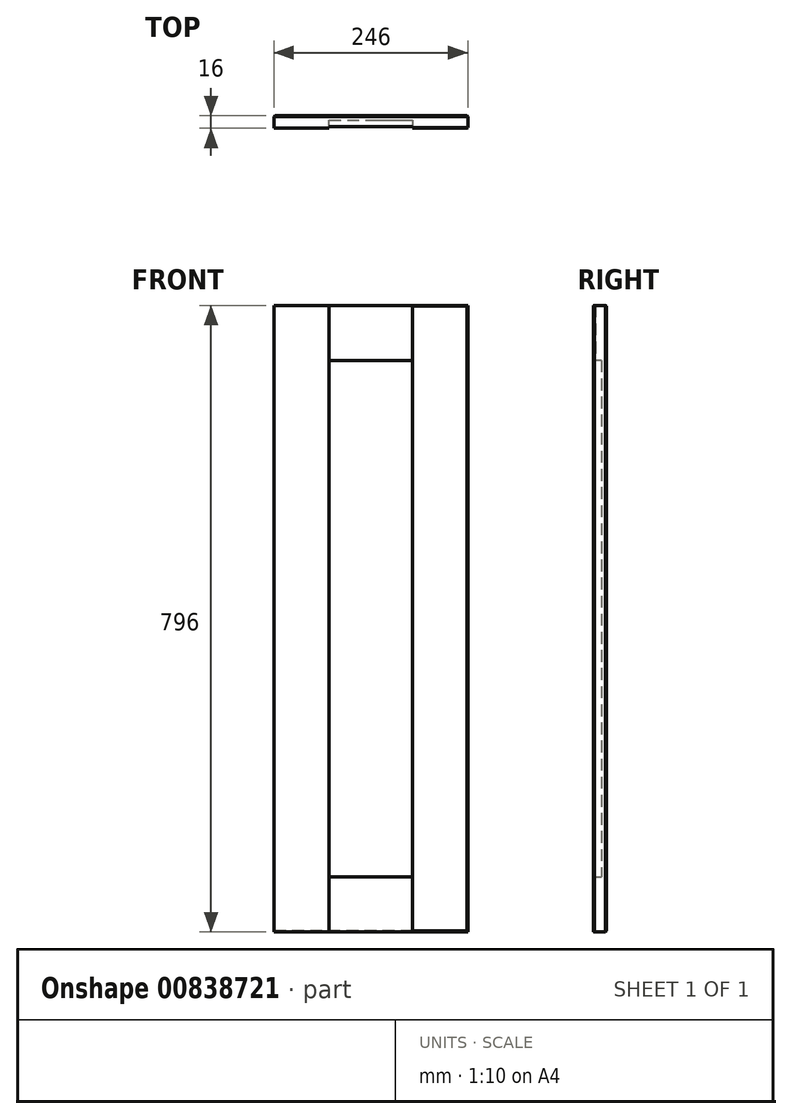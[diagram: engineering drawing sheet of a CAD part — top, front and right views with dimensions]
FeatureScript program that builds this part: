
annotation { "Feature Type Name" : "Feature", "Feature Type Description" : "" }
export const myFeature = defineFeature(function(context is Context, id is Id, definition is map)
    precondition{}
    {
        {
            var Q0;
            Q0=qCreatedBy(makeId("Front.planeOp"),FACE);
            var sketch = newSketch(context, id + "F0", { "sketchPlane" : qUnion([Q0])});
            skLineSegment(sketch, "E0.bottom", {"start": v(0, 0) * mm, "end": v(35.9, 0) * mm});
            skLineSegment(sketch, "E0.top", {"start": v(0, 30.12) * mm, "end": v(35.9, 30.12) * mm});
            skLineSegment(sketch, "E0.left", {"start": v(0, 0) * mm, "end": v(0, 30.12) * mm});
            skLineSegment(sketch, "E0.right", {"start": v(35.9, 0) * mm, "end": v(35.9, 30.12) * mm});
            skSolve(sketch);
        }
        {
            var Q0;
            Q0=makeQuery(id+"F0.imprint","IMPRINT",FACE,{"disambiguationData":[TD([[makeQuery(id+"F0.imprint","IMPRINT",EDGE,{"derivedFrom":sQuery(id+"F0.wireOp",EDGE,"E0.bottom")}),1.0]])]});
            extrude(context, id + "F1", {"entities" : qUnion([Q0]), "depth" : 16 * mm, "offsetDistance" : 25.4 * mm});
        }
        {
            var Q0;
            Q0=makeQuery(id+"F1.opExtrude","SWEPT_FACE",FACE,{"disambiguationData":[OSD([sQuery(id+"F0.wireOp",EDGE,"E0.left")])]});
            extrude(context, id + "F2", {"entities" : qUnion([Q0]), "operationType" : NewBodyOperationType.ADD, "oppositeDirection" : true, "depth" : 196 * mm, "offsetDistance" : 25 * mm});
        }
        {
            var Q0;
            {var subQ0=sQuery(id+"F0.wireOp",EDGE,"E0.bottom");Q0=makeQuery(id+"F2.boolean.opBoolean","MERGE",FACE,{"derivedFrom":[makeQuery(id+"F1.opExtrude","SWEPT_FACE",FACE,{"disambiguationData":[OSD([subQ0])]}),makeQuery(id+"F2.opExtrude","SWEPT_FACE",FACE,{"disambiguationData":[OSD([subQ0,sQuery(id+"F0.wireOp",EDGE,"E0.left")])]})]});}
            extrude(context, id + "F3", {"entities" : qUnion([Q0]), "operationType" : NewBodyOperationType.ADD, "oppositeDirection" : true, "depth" : 796 * mm, "offsetDistance" : 25 * mm});
        }
        {
            var Q0;
            {var subQ0=sQuery(id+"F0.wireOp",EDGE,"E0.left");var subQ1=sQuery(id+"F0.wireOp",EDGE,"E0.bottom");Q0=makeQuery(id+"F3.boolean.opBoolean","MERGE",FACE,{"derivedFrom":[makeQuery(id+"F2.boolean.opBoolean","MERGE",FACE,{"derivedFrom":[makeQuery(id+"F1.opExtrude","CAP_FACE",FACE,{"disambiguationData":[OSD([subQ1,sQuery(id+"F0.wireOp",EDGE,"E0.top"),subQ0,sQuery(id+"F0.wireOp",EDGE,"E0.right")])],"isStart":false}),makeQuery(id+"F2.opExtrude","SWEPT_FACE",FACE,{"disambiguationData":[OSD([subQ0]),TDD([makeQuery(id+"F1.opExtrude","CAP_EDGE",EDGE,{"disambiguationData":[OSD([subQ0])],"isStart":false})])]})]}),makeQuery(id+"F3.opExtrude","SWEPT_FACE",FACE,{"disambiguationData":[OSD([subQ1,subQ0]),TDD([makeQuery(id+"F2.boolean.opBoolean","MERGE",EDGE,{"derivedFrom":[makeQuery(id+"F1.opExtrude","CAP_EDGE",EDGE,{"disambiguationData":[OSD([subQ1])],"isStart":false}),makeQuery(id+"F2.opExtrude","SWEPT_EDGE",EDGE,{"disambiguationData":[OSD([subQ1,subQ0]),TDD([makeQuery(id+"F1.opExtrude","CAP_VERTEX",VERTEX,{"disambiguationData":[OSD([subQ1,subQ0])],"isStart":false})])]})]})])]})]});}
            var sketch = newSketch(context, id + "F4", { "sketchPlane" : qUnion([Q0])});
            skLineSegment(sketch, "E1.bottom", {"start": v(0, 796) * mm, "end": v(42.19, 796) * mm});
            skLineSegment(sketch, "E1.top", {"start": v(0, 751.57) * mm, "end": v(42.19, 751.57) * mm});
            skLineSegment(sketch, "E1.left", {"start": v(0, 796) * mm, "end": v(0, 751.57) * mm});
            skLineSegment(sketch, "E1.right", {"start": v(42.19, 796) * mm, "end": v(42.19, 751.57) * mm});
            skLineSegment(sketch, "E2.bottom", {"start": v(196, 796) * mm, "end": v(153.6, 796) * mm});
            skLineSegment(sketch, "E2.top", {"start": v(196, 746.75) * mm, "end": v(153.6, 746.75) * mm});
            skLineSegment(sketch, "E2.left", {"start": v(196, 796) * mm, "end": v(196, 746.75) * mm});
            skLineSegment(sketch, "E2.right", {"start": v(153.6, 796) * mm, "end": v(153.6, 746.75) * mm});
            skSolve(sketch);
        }
        {
            var Q0;
            Q0=makeQuery(id+"F4.imprint","IMPRINT",FACE,{"disambiguationData":[TD([[makeQuery(id+"F4.imprint","IMPRINT",EDGE,{"derivedFrom":sQuery(id+"F4.wireOp",EDGE,"E1.bottom")}),-1.0]])]});
            var Q1;
            Q1=makeQuery(id+"F4.imprint","IMPRINT",FACE,{"disambiguationData":[TD([[makeQuery(id+"F4.imprint","IMPRINT",EDGE,{"derivedFrom":sQuery(id+"F4.wireOp",EDGE,"E2.bottom")}),-1.0]])]});
            extrude(context, id + "F5", {"entities" : qUnion([Q0, Q1]), "operationType" : NewBodyOperationType.ADD, "depth" : 25 * mm, "offsetDistance" : 25 * mm});
        }
        {
            var Q0;
            {var subQ0=sQuery(id+"F0.wireOp",EDGE,"E0.left");var subQ1=sQuery(id+"F0.wireOp",EDGE,"E0.bottom");Q0=makeQuery(id+"F3.boolean.opBoolean","MERGE",FACE,{"derivedFrom":[makeQuery(id+"F2.boolean.opBoolean","MERGE",FACE,{"derivedFrom":[makeQuery(id+"F1.opExtrude","CAP_FACE",FACE,{"disambiguationData":[OSD([subQ1,sQuery(id+"F0.wireOp",EDGE,"E0.top"),subQ0,sQuery(id+"F0.wireOp",EDGE,"E0.right")])],"isStart":false}),makeQuery(id+"F2.opExtrude","SWEPT_FACE",FACE,{"disambiguationData":[OSD([subQ0]),TDD([makeQuery(id+"F1.opExtrude","CAP_EDGE",EDGE,{"disambiguationData":[OSD([subQ0])],"isStart":false})])]})]}),makeQuery(id+"F3.opExtrude","SWEPT_FACE",FACE,{"disambiguationData":[OSD([subQ1,subQ0]),TDD([makeQuery(id+"F2.boolean.opBoolean","MERGE",EDGE,{"derivedFrom":[makeQuery(id+"F1.opExtrude","CAP_EDGE",EDGE,{"disambiguationData":[OSD([subQ1])],"isStart":false}),makeQuery(id+"F2.opExtrude","SWEPT_EDGE",EDGE,{"disambiguationData":[OSD([subQ1,subQ0]),TDD([makeQuery(id+"F1.opExtrude","CAP_VERTEX",VERTEX,{"disambiguationData":[OSD([subQ1,subQ0])],"isStart":false})])]})]})])]})]});}
            var sketch = newSketch(context, id + "F6", { "sketchPlane" : qUnion([Q0])});
            skLineSegment(sketch, "E3.bottom", {"start": v(196, 0) * mm, "end": v(163.38, 0) * mm});
            skLineSegment(sketch, "E3.top", {"start": v(196, 46.55) * mm, "end": v(163.38, 46.55) * mm});
            skLineSegment(sketch, "E3.left", {"start": v(196, 0) * mm, "end": v(196, 46.55) * mm});
            skLineSegment(sketch, "E3.right", {"start": v(163.38, 0) * mm, "end": v(163.38, 46.55) * mm});
            skLineSegment(sketch, "E4.bottom", {"start": v(0, 0) * mm, "end": v(50.28, 0) * mm});
            skLineSegment(sketch, "E4.top", {"start": v(0, 44.4) * mm, "end": v(50.28, 44.4) * mm});
            skLineSegment(sketch, "E4.left", {"start": v(0, 0) * mm, "end": v(0, 44.4) * mm});
            skLineSegment(sketch, "E4.right", {"start": v(50.28, 0) * mm, "end": v(50.28, 44.4) * mm});
            skSolve(sketch);
        }
        {
            var Q0;
            Q0=makeQuery(id+"F6.imprint","IMPRINT",FACE,{"disambiguationData":[TD([[makeQuery(id+"F6.imprint","IMPRINT",EDGE,{"derivedFrom":sQuery(id+"F6.wireOp",EDGE,"E3.bottom")}),1.0]])]});
            var Q1;
            Q1=makeQuery(id+"F6.imprint","IMPRINT",FACE,{"disambiguationData":[TD([[makeQuery(id+"F6.imprint","IMPRINT",EDGE,{"derivedFrom":sQuery(id+"F6.wireOp",EDGE,"E4.bottom")}),1.0]])]});
            extrude(context, id + "F7", {"entities" : qUnion([Q0, Q1]), "operationType" : NewBodyOperationType.ADD, "depth" : 25 * mm, "offsetDistance" : 25 * mm});
        }
        {
            var Q0;
            Q0=makeQuery(id+"F7.opExtrude","SWEPT_FACE",FACE,{"disambiguationData":[OSD([sQuery(id+"F6.wireOp",EDGE,"E4.right")])]});
            extrude(context, id + "F8", {"entities" : qUnion([Q0]), "operationType" : NewBodyOperationType.ADD, "depth" : 19.72 * mm, "offsetDistance" : 25 * mm});
        }
        {
            var Q0;
            {var subQ0=sQuery(id+"F6.wireOp",EDGE,"E4.top");Q0=makeQuery(id+"F8.boolean.opBoolean","MERGE",FACE,{"derivedFrom":[makeQuery(id+"F7.opExtrude","SWEPT_FACE",FACE,{"disambiguationData":[OSD([subQ0])]}),makeQuery(id+"F8.opExtrude","SWEPT_FACE",FACE,{"disambiguationData":[OSD([subQ0,sQuery(id+"F6.wireOp",EDGE,"E4.right")])]})]});}
            extrude(context, id + "F9", {"entities" : qUnion([Q0]), "operationType" : NewBodyOperationType.ADD, "depth" : 25.6 * mm, "offsetDistance" : 25 * mm});
        }
        {
            var Q0;
            Q0=makeQuery(id+"F7.opExtrude","SWEPT_FACE",FACE,{"disambiguationData":[OSD([sQuery(id+"F6.wireOp",EDGE,"E3.right")])]});
            extrude(context, id + "F10", {"entities" : qUnion([Q0]), "operationType" : NewBodyOperationType.ADD, "depth" : 37.38 * mm, "offsetDistance" : 25 * mm});
        }
        {
            var Q0;
            {var subQ0=sQuery(id+"F6.wireOp",EDGE,"E3.top");Q0=makeQuery(id+"F10.boolean.opBoolean","MERGE",FACE,{"derivedFrom":[makeQuery(id+"F7.opExtrude","SWEPT_FACE",FACE,{"disambiguationData":[OSD([subQ0])]}),makeQuery(id+"F10.opExtrude","SWEPT_FACE",FACE,{"disambiguationData":[OSD([subQ0,sQuery(id+"F6.wireOp",EDGE,"E3.right")])]})]});}
            extrude(context, id + "F11", {"entities" : qUnion([Q0]), "operationType" : NewBodyOperationType.ADD, "depth" : 23.45 * mm, "offsetDistance" : 25 * mm});
        }
        {
            var Q0;
            Q0=makeQuery(id+"F5.opExtrude","SWEPT_FACE",FACE,{"disambiguationData":[OSD([sQuery(id+"F4.wireOp",EDGE,"E1.right")])]});
            extrude(context, id + "F12", {"entities" : qUnion([Q0]), "operationType" : NewBodyOperationType.ADD, "depth" : 27.8 * mm, "offsetDistance" : 25 * mm});
        }
        {
            var Q0;
            {var subQ0=sQuery(id+"F4.wireOp",EDGE,"E1.top");Q0=makeQuery(id+"F12.boolean.opBoolean","MERGE",FACE,{"derivedFrom":[makeQuery(id+"F5.opExtrude","SWEPT_FACE",FACE,{"disambiguationData":[OSD([subQ0])]}),makeQuery(id+"F12.opExtrude","SWEPT_FACE",FACE,{"disambiguationData":[OSD([subQ0,sQuery(id+"F4.wireOp",EDGE,"E1.right")])]})]});}
            extrude(context, id + "F13", {"entities" : qUnion([Q0]), "operationType" : NewBodyOperationType.ADD, "depth" : 25.57 * mm, "offsetDistance" : 25 * mm});
        }
        {
            var Q0;
            Q0=makeQuery(id+"F5.opExtrude","SWEPT_FACE",FACE,{"disambiguationData":[OSD([sQuery(id+"F4.wireOp",EDGE,"E2.top")])]});
            extrude(context, id + "F14", {"entities" : qUnion([Q0]), "operationType" : NewBodyOperationType.ADD, "depth" : 20.75 * mm, "offsetDistance" : 25 * mm});
        }
        {
            var Q0;
            {var subQ0=sQuery(id+"F4.wireOp",EDGE,"E2.right");Q0=makeQuery(id+"F14.boolean.opBoolean","MERGE",FACE,{"derivedFrom":[makeQuery(id+"F5.opExtrude","SWEPT_FACE",FACE,{"disambiguationData":[OSD([subQ0])]}),makeQuery(id+"F14.opExtrude","SWEPT_FACE",FACE,{"disambiguationData":[OSD([sQuery(id+"F4.wireOp",EDGE,"E2.top"),subQ0])]})]});}
            extrude(context, id + "F15", {"entities" : qUnion([Q0]), "operationType" : NewBodyOperationType.ADD, "depth" : 27.6 * mm, "offsetDistance" : 25 * mm});
        }
        {
            var Q0;
            {var subQ0=sQuery(id+"F0.wireOp",EDGE,"E0.left");var subQ1=sQuery(id+"F0.wireOp",EDGE,"E0.bottom");Q0=makeQuery(id+"F3.boolean.opBoolean","MERGE",FACE,{"derivedFrom":[makeQuery(id+"F2.boolean.opBoolean","MERGE",FACE,{"derivedFrom":[makeQuery(id+"F1.opExtrude","CAP_FACE",FACE,{"disambiguationData":[OSD([subQ1,sQuery(id+"F0.wireOp",EDGE,"E0.top"),subQ0,sQuery(id+"F0.wireOp",EDGE,"E0.right")])],"isStart":false}),makeQuery(id+"F2.opExtrude","SWEPT_FACE",FACE,{"disambiguationData":[OSD([subQ0]),TDD([makeQuery(id+"F1.opExtrude","CAP_EDGE",EDGE,{"disambiguationData":[OSD([subQ0])],"isStart":false})])]})]}),makeQuery(id+"F3.opExtrude","SWEPT_FACE",FACE,{"disambiguationData":[OSD([subQ1,subQ0]),TDD([makeQuery(id+"F2.boolean.opBoolean","MERGE",EDGE,{"derivedFrom":[makeQuery(id+"F1.opExtrude","CAP_EDGE",EDGE,{"disambiguationData":[OSD([subQ1])],"isStart":false}),makeQuery(id+"F2.opExtrude","SWEPT_EDGE",EDGE,{"disambiguationData":[OSD([subQ1,subQ0]),TDD([makeQuery(id+"F1.opExtrude","CAP_VERTEX",VERTEX,{"disambiguationData":[OSD([subQ1,subQ0])],"isStart":false})])]})]})])]})]});}
            var sketch = newSketch(context, id + "F16", { "sketchPlane" : qUnion([Q0])});
            skLineSegment(sketch, "E5.bottom", {"start": v(70, 726) * mm, "end": v(126, 726) * mm});
            skLineSegment(sketch, "E5.top", {"start": v(70, 70) * mm, "end": v(126, 70) * mm});
            skLineSegment(sketch, "E5.left", {"start": v(70, 726) * mm, "end": v(70, 70) * mm});
            skLineSegment(sketch, "E5.right", {"start": v(126, 726) * mm, "end": v(126, 70) * mm});
            skSolve(sketch);
        }
        {
            var Q0;
            Q0=makeQuery(id+"F16.imprint","IMPRINT",FACE,{"disambiguationData":[TD([[makeQuery(id+"F16.imprint","IMPRINT",EDGE,{"derivedFrom":sQuery(id+"F16.wireOp",EDGE,"E5.top")}),1.0]])]});
            extrude(context, id + "F17", {"entities" : qUnion([Q0]), "operationType" : NewBodyOperationType.REMOVE, "oppositeDirection" : true, "depth" : 10 * mm, "offsetDistance" : 25 * mm});
        }
        {
            var Q0;
            {var subQ2=sQuery(id+"F0.wireOp",EDGE,"E0.left");var subQ3=sQuery(id+"F0.wireOp",EDGE,"E0.bottom");var subQ4=makeQuery(id+"F1.opExtrude","CAP_FACE",FACE,{"disambiguationData":[OSD([subQ3,sQuery(id+"F0.wireOp",EDGE,"E0.top"),subQ2,sQuery(id+"F0.wireOp",EDGE,"E0.right")])],"isStart":false});var subQ7=makeQuery(id+"F3.opExtrude","SWEPT_FACE",FACE,{"disambiguationData":[OSD([subQ3,subQ2]),TDD([makeQuery(id+"F2.boolean.opBoolean","MERGE",EDGE,{"derivedFrom":[makeQuery(id+"F1.opExtrude","CAP_EDGE",EDGE,{"disambiguationData":[OSD([subQ3])],"isStart":false}),makeQuery(id+"F2.opExtrude","SWEPT_EDGE",EDGE,{"disambiguationData":[OSD([subQ3,subQ2]),TDD([makeQuery(id+"F1.opExtrude","CAP_VERTEX",VERTEX,{"disambiguationData":[OSD([subQ3,subQ2])],"isStart":false})])]})]})])]});var subQ8=makeQuery(id+"F2.opExtrude","SWEPT_FACE",FACE,{"disambiguationData":[OSD([subQ2]),TDD([makeQuery(id+"F1.opExtrude","CAP_EDGE",EDGE,{"disambiguationData":[OSD([subQ2])],"isStart":false})])]});Q0=makeQuery(id+"F17.boolean.opBoolean","SPLIT",FACE,{"disambiguationData":[TD([makeQuery(id+"F1.opExtrude","SWEPT_FACE",FACE,{"disambiguationData":[OSD([subQ3])]})])],"derivedFrom":makeQuery(id+"F3.boolean.opBoolean","MERGE",FACE,{"derivedFrom":[makeQuery(id+"F2.boolean.opBoolean","MERGE",FACE,{"derivedFrom":[subQ4,subQ8]}),subQ7]})});}
            var Q1;
            {var subQ2=sQuery(id+"F4.wireOp",EDGE,"E1.bottom");var subQ3=sQuery(id+"F0.wireOp",EDGE,"E0.left");var subQ4=sQuery(id+"F0.wireOp",EDGE,"E0.bottom");var subQ6=makeQuery(id+"F1.opExtrude","CAP_FACE",FACE,{"disambiguationData":[OSD([subQ4,sQuery(id+"F0.wireOp",EDGE,"E0.top"),subQ3,sQuery(id+"F0.wireOp",EDGE,"E0.right")])],"isStart":false});var subQ7=makeQuery(id+"F2.opExtrude","SWEPT_FACE",FACE,{"disambiguationData":[OSD([subQ3]),TDD([makeQuery(id+"F1.opExtrude","CAP_EDGE",EDGE,{"disambiguationData":[OSD([subQ3])],"isStart":false})])]});var subQ8=makeQuery(id+"F3.opExtrude","SWEPT_FACE",FACE,{"disambiguationData":[OSD([subQ4,subQ3]),TDD([makeQuery(id+"F2.boolean.opBoolean","MERGE",EDGE,{"derivedFrom":[makeQuery(id+"F1.opExtrude","CAP_EDGE",EDGE,{"disambiguationData":[OSD([subQ4])],"isStart":false}),makeQuery(id+"F2.opExtrude","SWEPT_EDGE",EDGE,{"disambiguationData":[OSD([subQ4,subQ3]),TDD([makeQuery(id+"F1.opExtrude","CAP_VERTEX",VERTEX,{"disambiguationData":[OSD([subQ4,subQ3])],"isStart":false})])]})]})])]});Q1=makeQuery(id+"F17.boolean.opBoolean","SPLIT",FACE,{"disambiguationData":[TD([makeQuery(id+"F5.opExtrude","SWEPT_FACE",FACE,{"disambiguationData":[OSD([subQ2])]})])],"derivedFrom":makeQuery(id+"F3.boolean.opBoolean","MERGE",FACE,{"derivedFrom":[makeQuery(id+"F2.boolean.opBoolean","MERGE",FACE,{"derivedFrom":[subQ6,subQ7]}),subQ8]})});}
            extrude(context, id + "F18", {"entities" : qUnion([Q0, Q1]), "operationType" : NewBodyOperationType.REMOVE, "oppositeDirection" : true, "depth" : 2 * mm, "offsetDistance" : 25 * mm});
        }
        {
            var Q0;
            {var subQ0=sQuery(id+"F4.wireOp",EDGE,"E1.right");var subQ1=sQuery(id+"F4.wireOp",EDGE,"E1.top");Q0=makeQuery(id+"F13.boolean.opBoolean","MERGE",FACE,{"derivedFrom":[makeQuery(id+"F12.boolean.opBoolean","MERGE",FACE,{"derivedFrom":[makeQuery(id+"F5.opExtrude","CAP_FACE",FACE,{"disambiguationData":[OSD([sQuery(id+"F4.wireOp",EDGE,"E1.bottom"),subQ1,sQuery(id+"F4.wireOp",EDGE,"E1.left"),subQ0])],"isStart":false}),makeQuery(id+"F12.opExtrude","SWEPT_FACE",FACE,{"disambiguationData":[OSD([subQ0]),TDD([makeQuery(id+"F5.opExtrude","CAP_EDGE",EDGE,{"disambiguationData":[OSD([subQ0])],"isStart":false})])]})]}),makeQuery(id+"F13.opExtrude","SWEPT_FACE",FACE,{"disambiguationData":[OSD([subQ1,subQ0]),TDD([makeQuery(id+"F12.boolean.opBoolean","MERGE",EDGE,{"derivedFrom":[makeQuery(id+"F5.opExtrude","CAP_EDGE",EDGE,{"disambiguationData":[OSD([subQ1])],"isStart":false}),makeQuery(id+"F12.opExtrude","SWEPT_EDGE",EDGE,{"disambiguationData":[OSD([subQ1,subQ0]),TDD([makeQuery(id+"F5.opExtrude","CAP_VERTEX",VERTEX,{"disambiguationData":[OSD([subQ1,subQ0])],"isStart":false})])]})]})])]})]});}
            var Q1;
            {var subQ0=sQuery(id+"F4.wireOp",EDGE,"E2.right");var subQ1=sQuery(id+"F4.wireOp",EDGE,"E2.top");Q1=makeQuery(id+"F15.boolean.opBoolean","MERGE",FACE,{"derivedFrom":[makeQuery(id+"F14.boolean.opBoolean","MERGE",FACE,{"derivedFrom":[makeQuery(id+"F5.opExtrude","CAP_FACE",FACE,{"disambiguationData":[OSD([sQuery(id+"F4.wireOp",EDGE,"E2.bottom"),subQ1,sQuery(id+"F4.wireOp",EDGE,"E2.left"),subQ0])],"isStart":false}),makeQuery(id+"F14.opExtrude","SWEPT_FACE",FACE,{"disambiguationData":[OSD([subQ1]),TDD([makeQuery(id+"F5.opExtrude","CAP_EDGE",EDGE,{"disambiguationData":[OSD([subQ1])],"isStart":false})])]})]}),makeQuery(id+"F15.opExtrude","SWEPT_FACE",FACE,{"disambiguationData":[OSD([subQ1,subQ0]),TDD([makeQuery(id+"F14.boolean.opBoolean","MERGE",EDGE,{"derivedFrom":[makeQuery(id+"F5.opExtrude","CAP_EDGE",EDGE,{"disambiguationData":[OSD([subQ0])],"isStart":false}),makeQuery(id+"F14.opExtrude","SWEPT_EDGE",EDGE,{"disambiguationData":[OSD([subQ1,subQ0]),TDD([makeQuery(id+"F5.opExtrude","CAP_VERTEX",VERTEX,{"disambiguationData":[OSD([subQ1,subQ0])],"isStart":false})])]})]})])]})]});}
            var Q2;
            {var subQ0=sQuery(id+"F6.wireOp",EDGE,"E4.right");var subQ1=sQuery(id+"F6.wireOp",EDGE,"E4.top");Q2=makeQuery(id+"F9.boolean.opBoolean","MERGE",FACE,{"derivedFrom":[makeQuery(id+"F8.boolean.opBoolean","MERGE",FACE,{"derivedFrom":[makeQuery(id+"F7.opExtrude","CAP_FACE",FACE,{"disambiguationData":[OSD([sQuery(id+"F6.wireOp",EDGE,"E4.bottom"),subQ1,sQuery(id+"F6.wireOp",EDGE,"E4.left"),subQ0])],"isStart":false}),makeQuery(id+"F8.opExtrude","SWEPT_FACE",FACE,{"disambiguationData":[OSD([subQ0]),TDD([makeQuery(id+"F7.opExtrude","CAP_EDGE",EDGE,{"disambiguationData":[OSD([subQ0])],"isStart":false})])]})]}),makeQuery(id+"F9.opExtrude","SWEPT_FACE",FACE,{"disambiguationData":[OSD([subQ1,subQ0]),TDD([makeQuery(id+"F8.boolean.opBoolean","MERGE",EDGE,{"derivedFrom":[makeQuery(id+"F7.opExtrude","CAP_EDGE",EDGE,{"disambiguationData":[OSD([subQ1])],"isStart":false}),makeQuery(id+"F8.opExtrude","SWEPT_EDGE",EDGE,{"disambiguationData":[OSD([subQ1,subQ0]),TDD([makeQuery(id+"F7.opExtrude","CAP_VERTEX",VERTEX,{"disambiguationData":[OSD([subQ1,subQ0])],"isStart":false})])]})]})])]})]});}
            var Q3;
            {var subQ0=sQuery(id+"F6.wireOp",EDGE,"E3.right");var subQ1=sQuery(id+"F6.wireOp",EDGE,"E3.top");Q3=makeQuery(id+"F11.boolean.opBoolean","MERGE",FACE,{"derivedFrom":[makeQuery(id+"F10.boolean.opBoolean","MERGE",FACE,{"derivedFrom":[makeQuery(id+"F7.opExtrude","CAP_FACE",FACE,{"disambiguationData":[OSD([sQuery(id+"F6.wireOp",EDGE,"E3.bottom"),subQ1,sQuery(id+"F6.wireOp",EDGE,"E3.left"),subQ0])],"isStart":false}),makeQuery(id+"F10.opExtrude","SWEPT_FACE",FACE,{"disambiguationData":[OSD([subQ0]),TDD([makeQuery(id+"F7.opExtrude","CAP_EDGE",EDGE,{"disambiguationData":[OSD([subQ0])],"isStart":false})])]})]}),makeQuery(id+"F11.opExtrude","SWEPT_FACE",FACE,{"disambiguationData":[OSD([subQ1,subQ0]),TDD([makeQuery(id+"F10.boolean.opBoolean","MERGE",EDGE,{"derivedFrom":[makeQuery(id+"F7.opExtrude","CAP_EDGE",EDGE,{"disambiguationData":[OSD([subQ1])],"isStart":false}),makeQuery(id+"F10.opExtrude","SWEPT_EDGE",EDGE,{"disambiguationData":[OSD([subQ1,subQ0]),TDD([makeQuery(id+"F7.opExtrude","CAP_VERTEX",VERTEX,{"disambiguationData":[OSD([subQ1,subQ0])],"isStart":false})])]})]})])]})]});}
            extrude(context, id + "F19", {"entities" : qUnion([Q0, Q1, Q2, Q3]), "operationType" : NewBodyOperationType.REMOVE, "oppositeDirection" : true, "depth" : 25 * mm, "offsetDistance" : 25 * mm});
        }
        {
            var Q0;
            {var subQ0=sQuery(id+"F4.wireOp",EDGE,"E2.left");var subQ1=sQuery(id+"F0.wireOp",EDGE,"E0.left");var subQ2=sQuery(id+"F0.wireOp",EDGE,"E0.bottom");var subQ3=sQuery(id+"F6.wireOp",EDGE,"E3.left");Q0=makeQuery(id+"F14.boolean.opBoolean","MERGE",FACE,{"derivedFrom":[makeQuery(id+"F11.boolean.opBoolean","MERGE",FACE,{"derivedFrom":[makeQuery(id+"F7.boolean.opBoolean","MERGE",FACE,{"derivedFrom":[makeQuery(id+"F5.boolean.opBoolean","MERGE",FACE,{"derivedFrom":[makeQuery(id+"F3.boolean.opBoolean","MERGE",FACE,{"derivedFrom":[makeQuery(id+"F2.opExtrude","CAP_FACE",FACE,{"disambiguationData":[OSD([subQ1])],"isStart":false}),makeQuery(id+"F3.opExtrude","SWEPT_FACE",FACE,{"disambiguationData":[OSD([subQ2,subQ1]),TDD([makeQuery(id+"F2.opExtrude","CAP_EDGE",EDGE,{"disambiguationData":[OSD([subQ2,subQ1])],"isStart":false})])]})]}),makeQuery(id+"F5.opExtrude","SWEPT_FACE",FACE,{"disambiguationData":[OSD([subQ0])]})]}),makeQuery(id+"F7.opExtrude","SWEPT_FACE",FACE,{"disambiguationData":[OSD([subQ3])]})]}),makeQuery(id+"F11.opExtrude","SWEPT_FACE",FACE,{"disambiguationData":[OSD([subQ2,subQ1,sQuery(id+"F6.wireOp",EDGE,"E3.top"),subQ3])]})]}),makeQuery(id+"F14.opExtrude","SWEPT_FACE",FACE,{"disambiguationData":[OSD([subQ2,subQ1,sQuery(id+"F4.wireOp",EDGE,"E2.top"),subQ0])]})]});}
            extrude(context, id + "F20", {"entities" : qUnion([Q0]), "operationType" : NewBodyOperationType.ADD, "depth" : 50 * mm, "offsetDistance" : 25 * mm});
        }
        {
            var Q0;
            {var subQ0=sQuery(id+"F4.wireOp",EDGE,"E2.right");var subQ1=sQuery(id+"F4.wireOp",EDGE,"E2.top");Q0=makeQuery(id+"F18.boolean.opBoolean","MERGE",FACE,{"derivedFrom":[makeQuery(id+"F15.opExtrude","CAP_FACE",FACE,{"disambiguationData":[OSD([subQ1,subQ0])],"isStart":false}),makeQuery(id+"F18.opExtrude","SWEPT_FACE",FACE,{"disambiguationData":[OSD([subQ1,subQ0])]})]});}
            var Q1;
            {var subQ0=sQuery(id+"F6.wireOp",EDGE,"E3.right");var subQ1=sQuery(id+"F6.wireOp",EDGE,"E3.top");Q1=makeQuery(id+"F18.boolean.opBoolean","MERGE",FACE,{"derivedFrom":[makeQuery(id+"F11.boolean.opBoolean","MERGE",FACE,{"derivedFrom":[makeQuery(id+"F10.opExtrude","CAP_FACE",FACE,{"disambiguationData":[OSD([subQ0])],"isStart":false}),makeQuery(id+"F11.opExtrude","SWEPT_FACE",FACE,{"disambiguationData":[OSD([subQ1,subQ0]),TDD([makeQuery(id+"F10.opExtrude","CAP_EDGE",EDGE,{"disambiguationData":[OSD([subQ1,subQ0])],"isStart":false})])]})]}),makeQuery(id+"F17.boolean.opBoolean","COPY",FACE,{"derivedFrom":makeQuery(id+"F17.opExtrude","SWEPT_FACE",FACE,{"disambiguationData":[OSD([sQuery(id+"F16.wireOp",EDGE,"E5.right")])]})}),makeQuery(id+"F18.opExtrude","SWEPT_FACE",FACE,{"disambiguationData":[OSD([subQ1,subQ0])]})]});}
            extrude(context, id + "F21", {"entities" : qUnion([Q0, Q1]), "operationType" : NewBodyOperationType.REMOVE, "oppositeDirection" : true, "depth" : 50 * mm, "offsetDistance" : 25 * mm});
        }
        {
            var Q0;
            Q0=makeQuery(id+"F19.boolean.opBoolean","COPY",EDGE,{"derivedFrom":makeQuery(id+"F19.opExtrude","CAP_EDGE",EDGE,{"disambiguationData":[OSD([sQuery(id+"F0.wireOp",EDGE,"E0.bottom"),sQuery(id+"F0.wireOp",EDGE,"E0.left"),sQuery(id+"F4.wireOp",EDGE,"E1.bottom"),sQuery(id+"F4.wireOp",EDGE,"E1.right")])],"isStart":false})});
            var Q1;
            {var subQ0=sQuery(id+"F4.wireOp",EDGE,"E2.bottom");Q1=makeQuery(id+"F20.boolean.opBoolean","MERGE",EDGE,{"derivedFrom":[makeQuery(id+"F19.boolean.opBoolean","COPY",EDGE,{"derivedFrom":makeQuery(id+"F19.opExtrude","CAP_EDGE",EDGE,{"disambiguationData":[OSD([sQuery(id+"F0.wireOp",EDGE,"E0.bottom"),sQuery(id+"F0.wireOp",EDGE,"E0.left"),subQ0,sQuery(id+"F4.wireOp",EDGE,"E2.right")])],"isStart":false})}),makeQuery(id+"F20.opExtrude","SWEPT_EDGE",EDGE,{"disambiguationData":[OSD([subQ0,sQuery(id+"F4.wireOp",EDGE,"E2.left")])]})]});}
            var Q2;
            Q2=makeQuery(id+"F20.opExtrude","CAP_EDGE",EDGE,{"disambiguationData":[OSD([sQuery(id+"F0.wireOp",EDGE,"E0.bottom"),sQuery(id+"F0.wireOp",EDGE,"E0.left"),sQuery(id+"F4.wireOp",EDGE,"E2.top"),sQuery(id+"F4.wireOp",EDGE,"E2.left"),sQuery(id+"F6.wireOp",EDGE,"E3.top"),sQuery(id+"F6.wireOp",EDGE,"E3.left")])],"isStart":false});
            var Q3;
            {var subQ0=sQuery(id+"F0.wireOp",EDGE,"E0.left");var subQ1=sQuery(id+"F0.wireOp",EDGE,"E0.bottom");Q3=makeQuery(id+"F19.boolean.opBoolean","MERGE",EDGE,{"derivedFrom":[makeQuery(id+"F3.boolean.opBoolean","MERGE",EDGE,{"derivedFrom":[makeQuery(id+"F1.opExtrude","CAP_EDGE",EDGE,{"disambiguationData":[OSD([subQ0])],"isStart":false}),makeQuery(id+"F3.opExtrude","SWEPT_EDGE",EDGE,{"disambiguationData":[OSD([subQ1,subQ0]),TDD([makeQuery(id+"F1.opExtrude","CAP_VERTEX",VERTEX,{"disambiguationData":[OSD([subQ1,subQ0])],"isStart":false})])]})]}),makeQuery(id+"F19.opExtrude","CAP_EDGE",EDGE,{"disambiguationData":[OSD([subQ1,subQ0,sQuery(id+"F6.wireOp",EDGE,"E4.top"),sQuery(id+"F6.wireOp",EDGE,"E4.left")])],"isStart":false}),makeQuery(id+"F19.opExtrude","CAP_EDGE",EDGE,{"disambiguationData":[OSD([subQ1,subQ0,sQuery(id+"F4.wireOp",EDGE,"E1.top"),sQuery(id+"F4.wireOp",EDGE,"E1.left")])],"isStart":false})]});}
            var Q4;
            {var subQ0=sQuery(id+"F6.wireOp",EDGE,"E3.bottom");Q4=makeQuery(id+"F20.boolean.opBoolean","MERGE",EDGE,{"derivedFrom":[makeQuery(id+"F19.boolean.opBoolean","COPY",EDGE,{"derivedFrom":makeQuery(id+"F19.opExtrude","CAP_EDGE",EDGE,{"disambiguationData":[OSD([sQuery(id+"F0.wireOp",EDGE,"E0.bottom"),sQuery(id+"F0.wireOp",EDGE,"E0.left"),subQ0,sQuery(id+"F6.wireOp",EDGE,"E3.right")])],"isStart":false})}),makeQuery(id+"F20.opExtrude","SWEPT_EDGE",EDGE,{"disambiguationData":[OSD([subQ0,sQuery(id+"F6.wireOp",EDGE,"E3.left")])]})]});}
            var Q5;
            Q5=makeQuery(id+"F19.boolean.opBoolean","COPY",EDGE,{"derivedFrom":makeQuery(id+"F19.opExtrude","CAP_EDGE",EDGE,{"disambiguationData":[OSD([sQuery(id+"F0.wireOp",EDGE,"E0.bottom"),sQuery(id+"F0.wireOp",EDGE,"E0.left"),sQuery(id+"F6.wireOp",EDGE,"E4.bottom"),sQuery(id+"F6.wireOp",EDGE,"E4.right")])],"isStart":false})});
            var Q6;
            {var subQ0=sQuery(id+"F0.wireOp",EDGE,"E0.left");var subQ1=sQuery(id+"F0.wireOp",EDGE,"E0.bottom");Q6=makeQuery(id+"F20.boolean.opBoolean","MERGE",FACE,{"derivedFrom":[makeQuery(id+"F3.boolean.opBoolean","MERGE",FACE,{"derivedFrom":[makeQuery(id+"F2.boolean.opBoolean","MERGE",FACE,{"derivedFrom":[makeQuery(id+"F1.opExtrude","CAP_FACE",FACE,{"disambiguationData":[OSD([subQ1,sQuery(id+"F0.wireOp",EDGE,"E0.top"),subQ0,sQuery(id+"F0.wireOp",EDGE,"E0.right")])],"isStart":true}),makeQuery(id+"F2.opExtrude","SWEPT_FACE",FACE,{"disambiguationData":[OSD([subQ0]),TDD([makeQuery(id+"F1.opExtrude","CAP_EDGE",EDGE,{"disambiguationData":[OSD([subQ0])],"isStart":true})])]})]}),makeQuery(id+"F3.opExtrude","SWEPT_FACE",FACE,{"disambiguationData":[OSD([subQ1,subQ0]),TDD([makeQuery(id+"F2.boolean.opBoolean","MERGE",EDGE,{"derivedFrom":[makeQuery(id+"F1.opExtrude","CAP_EDGE",EDGE,{"disambiguationData":[OSD([subQ1])],"isStart":true}),makeQuery(id+"F2.opExtrude","SWEPT_EDGE",EDGE,{"disambiguationData":[OSD([subQ1,subQ0]),TDD([makeQuery(id+"F1.opExtrude","CAP_VERTEX",VERTEX,{"disambiguationData":[OSD([subQ1,subQ0])],"isStart":true})])]})]})])]})]}),makeQuery(id+"F20.opExtrude","SWEPT_FACE",FACE,{"disambiguationData":[OSD([subQ1,subQ0])]})]});}
            chamfer(context, id + "F22", {"entities" : qUnion([Q0, Q1, Q2, Q3, Q4, Q5, Q6]), "width" : 1 * mm, "tangentPropagation" : true});
        }
    });
